FCSTD DOCUMENT  (FreeCAD 1.0RUnknown)
Label: wardrobe_corpus00_jan_assy4
License: All rights reserved
objects: App::Link×8, App::DocumentObjectGroup×3, Part::FeaturePython×3, PartDesign::CoordinateSystem×2, App::FeaturePython×1, App::Part×1
note: 5 computed .brp shape members not serialized (recipe doc carries the construction recipe); baked Part::Feature solids carry a one-line shape summary decoded from their .brp
EXTERNAL_REF file=parts/wardrobe_base_jan.FCStd obj=LCS_center
EXTERNAL_REF file=parts/wardrobe_base_jan.FCStd obj=Body
EXTERNAL_REF file=parts/wardrobe_base_jan.FCStd obj=LCS_1
EXTERNAL_REF file=parts/wardrobe_left_corpus00_jan.FCStd obj=LCS_bottom
EXTERNAL_REF file=parts/wardrobe_left_corpus00_jan.FCStd obj=Body001
EXTERNAL_REF file=parts/wardrobe_base_jan.FCStd obj=LCS_right
EXTERNAL_REF file=parts/wardrobe_right_corpus00_jan.FCStd obj=LCS_bottom
EXTERNAL_REF file=parts/wardrobe_right_corpus00_jan.FCStd obj=Body002
EXTERNAL_REF file=parts/wardrobe_left_corpus00_jan.FCStd obj=LCS_top
EXTERNAL_REF file=parts/wardrobe_top_jan.FCStd obj=LCS_left
EXTERNAL_REF file=parts/wardrobe_top_jan.FCStd obj=Body003
EXTERNAL_REF file=parts/wardrobe_backplate_corpus00_jan.FCStd obj=LCS_bottom
EXTERNAL_REF file=parts/wardrobe_base_jan.FCStd obj=LCS_back
EXTERNAL_REF file=parts/wardrobe_backplate_corpus00_jan.FCStd obj=Body004
EXTERNAL_REF file=parts/wardrobe_base_jan.FCStd obj=LCS_door
EXTERNAL_REF file=parts/wardrobe_door_corpus00_jan.FCStd obj=Body
EXTERNAL_REF file=wardrobe_drawer_jan_assy4.FCStd obj=LCS_Origin
EXTERNAL_REF file=parts/wardrobe_left_corpus00_jan.FCStd obj=LCS_inner_bottom
EXTERNAL_REF file=wardrobe_drawer_jan_assy4.FCStd obj=Assembly
EXTERNAL_REF file=../purchased parts/hettich-level-adjustment.FCStd obj=LCS_Origin
EXTERNAL_REF file=parts/wardrobe_base_jan.FCStd obj=LCS_2
EXTERNAL_REF file=../purchased parts/hettich-level-adjustment.FCStd obj=hettich_level_adjustment

FEATURE [App::DocumentObjectGroup] Parts
FEATURE [PartDesign::CoordinateSystem] LCS_Origin
  AttacherType = Attacher::AttachEngine3D
  AttachmentSupport = -> [X_Axis]
  MapMode = 2
FEATURE [App::DocumentObjectGroup] Constraints
FEATURE [App::FeaturePython] Variables  # WARN: FeaturePython — macro-defined, semantics opaque (R4)
  Type = App::PropertyContainer
FEATURE [App::DocumentObjectGroup] Configurations
FEATURE [App::Link] wardrobe_base_jan
  AttachedBy = #LCS_center
  AttachedTo = Parent Assembly#LCS_Origin
  LinkedObject = -> <external parts/wardrobe_base_jan.FCStd>#Body
  SolverId = Asm4EE
  expr: Placement = LCS_Origin.Placement * AttachmentOffset * wardrobe_base_jan#LCS_center.Placement ^ -1
FEATURE [App::Link] wardrobe_left_corpus00_jan
  AttachedBy = #LCS_bottom
  AttachedTo = wardrobe_base_jan#LCS_1
  LinkPlacement = pos=(-270,2.37e-13,1022.5) rot=(0,0,1;0rad)
  LinkedObject = -> <external parts/wardrobe_left_corpus00_jan.FCStd>#Body001
  Placement = pos=(-270,2.37e-13,1022.5) rot=(0,0,1;0rad)
  SolverId = Asm4EE
  expr: Placement = wardrobe_base_jan.Placement * wardrobe_base_jan#LCS_1.Placement * AttachmentOffset * wardrobe_left_corpus00_jan#LCS_bottom.Placement ^ -1
FEATURE [App::Link] wardrobe_right_corpus00_jan
  AttachedBy = #LCS_bottom
  AttachedTo = wardrobe_base_jan#LCS_right
  LinkPlacement = pos=(251,2.086e-13,1022.5) rot=(0,0,1;0rad)
  LinkedObject = -> <external parts/wardrobe_right_corpus00_jan.FCStd>#Body002
  Placement = pos=(251,2.086e-13,1022.5) rot=(0,0,1;0rad)
  SolverId = Asm4EE
  expr: Placement = wardrobe_base_jan.Placement * wardrobe_base_jan#LCS_right.Placement * AttachmentOffset * wardrobe_right_corpus00_jan#LCS_bottom.Placement ^ -1
FEATURE [App::Link] wardrobe_top_jan
  AttachedBy = #LCS_left
  AttachedTo = wardrobe_left_corpus00_jan#LCS_top
  LinkPlacement = pos=(-5.116e-13,3.858e-13,2026) rot=(0,0,1;0rad)
  LinkedObject = -> <external parts/wardrobe_top_jan.FCStd>#Body003
  Placement = pos=(-5.116e-13,3.858e-13,2026) rot=(0,0,1;0rad)
  SolverId = Asm4EE
  expr: Placement = wardrobe_left_corpus00_jan.Placement * wardrobe_left_corpus00_jan#LCS_top.Placement * AttachmentOffset * wardrobe_top_jan#LCS_left.Placement ^ -1
FEATURE [App::Link] wardrobe_backplate_corpus00_jan
  AttachedBy = #LCS_bottom
  AttachedTo = wardrobe_base_jan#LCS_back
  LinkPlacement = pos=(5.68e-14,319,1022.5) rot=(0,0,1;0rad)
  LinkedObject = -> <external parts/wardrobe_backplate_corpus00_jan.FCStd>#Body004
  Placement = pos=(5.68e-14,319,1022.5) rot=(0,0,1;0rad)
  SolverId = Asm4EE
  expr: Placement = wardrobe_base_jan.Placement * wardrobe_base_jan#LCS_back.Placement * AttachmentOffset * wardrobe_backplate_corpus00_jan#LCS_bottom.Placement ^ -1
FEATURE [App::Link] wardrobe_door_corpus00_jan
  AttachedBy = #LCS_right
  AttachedTo = wardrobe_base_jan#LCS_door
  AttachmentOffset = pos=(2.5,0,0) rot=(0,0,1;1.5708rad)
  LinkPlacement = pos=(267.5,-300,0) rot=(0.57735,0.57735,0.57735;2.0944rad)
  LinkedObject = -> <external parts/wardrobe_door_corpus00_jan.FCStd>#Body
  Placement = pos=(267.5,-300,0) rot=(0.57735,0.57735,0.57735;2.0944rad)
  SolverId = Asm4EE
  expr: Placement = wardrobe_base_jan.Placement * wardrobe_base_jan#LCS_door.Placement * AttachmentOffset * wardrobe_door_corpus00_jan#LCS_right.Placement ^ -1
FEATURE [App::Link] wardrobe_drawer_jan_assy4
  AttachedBy = #LCS_Origin
  AttachedTo = wardrobe_left_corpus00_jan#LCS_inner_bottom
  AttachmentOffset = pos=(0,20,0) rot=(0,0,1;1.5708rad)
  LinkPlacement = pos=(-251,2.232e-13,39) rot=(0.57735,0.57735,0.57735;4.18879rad)
  LinkedObject = -> <external wardrobe_drawer_jan_assy4.FCStd>#Assembly
  Placement = pos=(-251,2.232e-13,39) rot=(0.57735,0.57735,0.57735;4.18879rad)
  SolverId = Asm4EE
  expr: Placement = wardrobe_left_corpus00_jan.Placement * wardrobe_left_corpus00_jan#LCS_inner_bottom.Placement * AttachmentOffset * wardrobe_drawer_jan_assy4#LCS_Origin.Placement ^ -1
FEATURE [Part::FeaturePython] Linear_wardrobe_drawer_jan_assy4  # Draft array (typed FeaturePython)
  ArrayType = Linear Array
  Axis = -> Z_Axis
  AxisPlacement = pos=(0,0,0) rot=(0,0,1.73205;3.14159rad)
  Count = 6
  Index = 1
  LinearStep = 200
  PlacementList = 6 placements: arithmetic series from (-251,2.2323e-13,39) step (5.68434e-14,0,200) to (-251,2.2323e-13,1039)
  Placer = pos=(0,0,1000) rot=(0,0,1;0rad)
  ScaleList = (6) [(1,1,1),(1,1,1),(1,1,1),(1,1,1),(1,1,1),(1,1,1)]
  Scaler = 1
  ShowElement = false
  SourceObject = -> wardrobe_drawer_jan_assy4
  expr: .Placer.Base.z = LinearStep * Index
FEATURE [PartDesign::CoordinateSystem] LCS_003  label="LCS_1"
  AttacherType = Attacher::AttachEngine3D
FEATURE [App::Link] hettich_level_adjustment
  AttachedBy = #LCS_Origin
  AttachedTo = wardrobe_base_jan#LCS_2
  AttachmentOffset = pos=(0,0,0) rot=(0.707107,-0.707107,0;3.14159rad)
  LinkPlacement = pos=(-220,-230,0) rot=(0.707107,-0.707107,0;3.14159rad)
  LinkedObject = -> <external ../purchased parts/hettich-level-adjustment.FCStd>#hettich_level_adjustment
  Placement = pos=(-220,-230,0) rot=(0.707107,-0.707107,0;3.14159rad)
  SolverId = Asm4EE
  expr: Placement = wardrobe_base_jan.Placement * wardrobe_base_jan#LCS_2.Placement * AttachmentOffset * hettich_level_adjustment#LCS_Origin.Placement ^ -1
FEATURE [Part::FeaturePython] Linear_hettich_level_adjustment  # Draft array (typed FeaturePython)
  ArrayType = Linear Array
  Axis = -> X_Axis
  AxisPlacement = pos=(0,0,0) rot=(0.57735,0.57735,0.57735;2.0944rad)
  Count = 2
  Index = 1
  LinearStep = 440
  PlacementList = 2 placements: [(-220,-230,6.31089e-30),(220,-230,4.88498e-14)]
  Placer = pos=(0,0,440) rot=(0,0,1;0rad)
  ScaleList = (2) [(1,1,1),(1,1,1)]
  Scaler = 1
  ShowElement = false
  SourceObject = -> hettich_level_adjustment
  expr: .Placer.Base.z = LinearStep * Index
FEATURE [Part::FeaturePython] Linear_Linear_hettich_level_adjustment  # Draft array (typed FeaturePython)
  ArrayType = Linear Array
  Axis = -> Y_Axis
  AxisPlacement = pos=(0,0,0) rot=(1,1,1;4.18879rad)
  Count = 2
  Index = 1
  LinearStep = 460
  PlacementList = 2 placements: [(0,0,0),(5.10703e-14,460,-1.53211e-13)]
  Placer = pos=(0,0,460) rot=(0,0,1;0rad)
  ScaleList = (2) [(1,1,1),(1,1,1)]
  Scaler = 1
  ShowElement = false
  SourceObject = -> Linear_hettich_level_adjustment
  expr: .Placer.Base.z = LinearStep * Index
FEATURE [App::Part] Assembly  label="wardrobe_corpus00_jan"
  AssemblyType = Part::Link
  Group = -> [LCS_Origin,Constraints,Variables,Configurations,wardrobe_base_jan,wardrobe_left_corpus00_jan,wardrobe_right_corpus00_jan,wardrobe_top_jan,wardrobe_backplate_corpus00_jan,wardrobe_door_corpus00_jan,wardrobe_drawer_jan_assy4,Linear_wardrobe_drawer_jan_assy4,LCS_003,hettich_level_adjustment,Linear_hettich_level_adjustment,Linear_Linear_hettich_level_adjustment]
  Origin = -> Origin
  Type = Assembly

RESOLVED EXTERNAL PARTS (link-assembly join: the EXTERNAL_REF files above that resolve inside this repo's crawl, each included once):
---- part parts/wardrobe_backplate_corpus00_jan.FCStd = doc fcstd_ef48b797989f ----
FCSTD DOCUMENT  (FreeCAD 1.0RUnknown)
Label: wardrobe_backplate_corpus00_jan
License: All rights reserved
LicenseURL: https://en.wikipedia.org/wiki/All_rights_reserved
objects: PartDesign::CoordinateSystem×2, Sketcher::SketchObject×1, PartDesign::Pad×1, PartDesign::Body×1
note: 8 computed .brp shape members not serialized (recipe doc carries the construction recipe); baked Part::Feature solids carry a one-line shape summary decoded from their .brp
EXTERNAL_REF file=../../mastersketch.FCStd obj=Spreadsheet

FEATURE [Sketcher::SketchObject] Sketch004
  ArcFitTolerance = 1e-06
  AttachmentSupport = -> [XZ_Plane006]
  FullyConstrained = true
  MakeInternals = false
  MapMode = 5
  Placement = pos=(0,0,0) rot=(1,0,0;1.5708rad)
  expr: Constraints[10] = mastersketch#Spreadsheet.corpus_width
  expr: Constraints[11] = mastersketch#Spreadsheet.corpus_height
  sketch-geometry (5):
    g0: LineSegment StartX=-270 StartY=-1022.5 StartZ=0 EndX=270 EndY=-1022.5 EndZ=0
    g1: LineSegment StartX=270 StartY=-1022.5 StartZ=0 EndX=270 EndY=1022.5 EndZ=0
    g2: LineSegment StartX=270 StartY=1022.5 StartZ=0 EndX=-270 EndY=1022.5 EndZ=0
    g3: LineSegment StartX=-270 StartY=1022.5 StartZ=0 EndX=-270 EndY=-1022.5 EndZ=0
    g4: GeomPoint [constr] X=0 Y=0 Z=0
  constraints (12):
    c: Coincident(g0,g1)
    c: Coincident(g1,g2)
    c: Coincident(g2,g3)
    c: Coincident(g3,g0)
    c: Horizontal(g0)
    c: Horizontal(g2)
    c: Vertical(g1)
    c: Vertical(g3)
    c: Symmetric(g2,g0,g4)
    c: Coincident(g4,g-1)
    c: DistanceX(g0,g0) = 540
    c: DistanceY(g3,g3) = 2045
FEATURE [PartDesign::Pad] Pad004
  Direction = (0,-1,2e-16)
  Length = 19
  Length2 = 10
  Placement = pos=(0,0,0) rot=(1,0,0;1.5708rad)
  Profile = -> Sketch004
  ReferenceAxis = -> Sketch004 [N_Axis]
  Refine = true
  Suppressed = false
  Type = 0
  expr: Length = mastersketch#Spreadsheet.corpus_backplate_thickness
FEATURE [PartDesign::CoordinateSystem] LCS_bottom
  AttacherType = Attacher::AttachEngine3D
  AttachmentSupport = -> [Pad004]
  MapMode = 45
  Placement = pos=(0,-19,-1022.5) rot=(0.57735,0.57735,0.57735;2.0944rad)
FEATURE [PartDesign::CoordinateSystem] LCS_back_right
  AttacherType = Attacher::AttachEngine3D
FEATURE [PartDesign::Body] Body004  label="wardrobe_backplate_corpus00_jan"
  AllowCompound = false
  Group = -> [Sketch004,Pad004,LCS_bottom,LCS_back_right]
  Origin = -> Origin006
  Tip = -> Pad004
---- part parts/wardrobe_base_jan.FCStd = doc fcstd_ceb563eaf676 ----
FCSTD DOCUMENT  (FreeCAD 1.0RUnknown)
Label: wardrobe_base_jan
License: All rights reserved
LicenseURL: https://en.wikipedia.org/wiki/All_rights_reserved
objects: PartDesign::CoordinateSystem×9, Sketcher::SketchObject×2, PartDesign::Pad×1, PartDesign::Body×1
note: 17 computed .brp shape members not serialized (recipe doc carries the construction recipe); baked Part::Feature solids carry a one-line shape summary decoded from their .brp
EXTERNAL_REF file=../../mastersketch.FCStd obj=Spreadsheet

FEATURE [Sketcher::SketchObject] Sketch
  ArcFitTolerance = 1e-06
  AttachmentSupport = -> [XY_Plane]
  FullyConstrained = true
  MakeInternals = false
  MapMode = 5
  expr: Constraints[10] = mastersketch#Spreadsheet.corpus_width
  expr: Constraints[11] = mastersketch#Spreadsheet.corpus_depth
  sketch-geometry (5):
    g0: LineSegment StartX=-270 StartY=-300 StartZ=0 EndX=270 EndY=-300 EndZ=0
    g1: LineSegment StartX=270 StartY=-300 StartZ=0 EndX=270 EndY=300 EndZ=0
    g2: LineSegment StartX=270 StartY=300 StartZ=0 EndX=-270 EndY=300 EndZ=0
    g3: LineSegment StartX=-270 StartY=300 StartZ=0 EndX=-270 EndY=-300 EndZ=0
    g4: GeomPoint [constr] X=0 Y=0 Z=0
  constraints (12):
    c: Coincident(g0,g1)
    c: Coincident(g1,g2)
    c: Coincident(g2,g3)
    c: Coincident(g3,g0)
    c: Horizontal(g0)
    c: Horizontal(g2)
    c: Vertical(g1)
    c: Vertical(g3)
    c: Symmetric(g2,g0,g4)
    c: Coincident(g4,g-1)
    c: DistanceX(g0,g0) = 540
    c: DistanceY(g3,g3) = 600
FEATURE [PartDesign::Pad] Pad
  Direction = (0,0,1)
  Length = 19
  Length2 = 10
  Profile = -> Sketch
  ReferenceAxis = -> Sketch [N_Axis]
  Refine = true
  Suppressed = false
  Type = 0
  expr: Length = mastersketch#Spreadsheet.corpus_outer_thickness
FEATURE [PartDesign::CoordinateSystem] LCS_1  label="LCS_left"
  AttacherType = Attacher::AttachEngine3D
  AttachmentSupport = -> [Pad]
  MapMode = 45
  Placement = pos=(-270,1.42e-14,19) rot=(0,0.707107,0.707107;3.14159rad)
FEATURE [PartDesign::CoordinateSystem] LCS_right  label="LCS-right"
  AttacherType = Attacher::AttachEngine3D
  AttachmentSupport = -> [Pad]
  MapMode = 45
  Placement = pos=(270,-1.42e-14,19) rot=(0,0.707107,0.707107;3.14159rad)
FEATURE [PartDesign::CoordinateSystem] LCS_center
  AttacherType = Attacher::AttachEngine3D
FEATURE [Sketcher::SketchObject] Sketch_1  label="feet_placement"
  ArcFitTolerance = 1e-06
  AttachmentSupport = -> [Pad]
  FullyConstrained = true
  MakeInternals = false
  MapMode = 5
  Placement = pos=(0,0,0) rot=(1,0,0;3.14159rad)
  expr: Constraints[10] = mastersketch#Spreadsheet.corpus_width - 100
  expr: Constraints[11] = mastersketch#Spreadsheet.corpus_depth - 140
  sketch-geometry (5):
    g0: LineSegment StartX=-220 StartY=-230 StartZ=0 EndX=220 EndY=-230 EndZ=0
    g1: LineSegment StartX=220 StartY=-230 StartZ=0 EndX=220 EndY=230 EndZ=0
    g2: LineSegment StartX=220 StartY=230 StartZ=0 EndX=-220 EndY=230 EndZ=0
    g3: LineSegment StartX=-220 StartY=230 StartZ=0 EndX=-220 EndY=-230 EndZ=0
    g4: GeomPoint [constr] X=0 Y=0 Z=0
  constraints (12):
    c: Coincident(g0,g1)
    c: Coincident(g1,g2)
    c: Coincident(g2,g3)
    c: Coincident(g3,g0)
    c: Horizontal(g0)
    c: Horizontal(g2)
    c: Vertical(g1)
    c: Vertical(g3)
    c: Symmetric(g2,g0,g4)
    c: Coincident(g4,g-1)
    c: DistanceX(g0,g0) = 440
    c: DistanceY(g3,g3) = 460
FEATURE [PartDesign::CoordinateSystem] LCS_2  label="LCS_feet0"
  AttacherType = Attacher::AttachEngine3D
  AttachmentSupport = -> [Sketch_1]
  MapMode = 1
  Placement = pos=(-220,-230,0) rot=(0,0,1;0rad)
FEATURE [PartDesign::CoordinateSystem] LCS_feet1
  AttacherType = Attacher::AttachEngine3D
  AttachmentSupport = -> [Sketch_1]
  MapMode = 1
  Placement = pos=(220,-230,0) rot=(0,0,1;0rad)
FEATURE [PartDesign::CoordinateSystem] LCS_feet2
  AttacherType = Attacher::AttachEngine3D
  AttachmentSupport = -> [Sketch_1]
  MapMode = 1
  Placement = pos=(220,230,0) rot=(0,0,1;0rad)
FEATURE [PartDesign::CoordinateSystem] LCS_feet3
  AttacherType = Attacher::AttachEngine3D
  AttachmentSupport = -> [Sketch_1]
  MapMode = 1
  Placement = pos=(-220,230,0) rot=(0,0,1;0rad)
FEATURE [PartDesign::CoordinateSystem] LCS_back
  AttacherType = Attacher::AttachEngine3D
  AttachmentSupport = -> [Pad]
  MapMode = 45
  Placement = pos=(0,300,0) rot=(0.57735,0.57735,0.57735;2.0944rad)
FEATURE [PartDesign::CoordinateSystem] LCS_door
  AttacherType = Attacher::AttachEngine3D
  AttachmentSupport = -> [Pad]
  MapMode = 7
  Placement = pos=(270,-300,0) rot=(0,1,0;3.14159rad)
FEATURE [PartDesign::Body] Body  label="wardrobe_base_jan"
  AllowCompound = false
  Group = -> [Sketch,Pad,LCS_1,LCS_right,LCS_center,Sketch_1,LCS_2,LCS_feet1,LCS_feet2,LCS_feet3,LCS_back,LCS_door]
  Origin = -> Origin
  Tip = -> Pad
---- part parts/wardrobe_door_corpus00_jan.FCStd = doc fcstd_de45f609bab9 ----
FCSTD DOCUMENT  (FreeCAD 1.0R39285 (Git))
Label: wardrobe_door_corpus00_jan
License: All rights reserved
LicenseURL: https://en.wikipedia.org/wiki/All_rights_reserved
objects: TechDraw::DrawViewDimension×7, PartDesign::CoordinateSystem×2, TechDraw::DrawProjGroupItem×2, Sketcher::SketchObject×1, PartDesign::Pad×1, PartDesign::Body×1, TechDraw::DrawSVGTemplate×1, TechDraw::DrawViewAnnotation×1, App::Part×1, TechDraw::DrawPage×1
note: 17 computed .brp shape members not serialized (recipe doc carries the construction recipe); baked Part::Feature solids carry a one-line shape summary decoded from their .brp
EXTERNAL_REF file=../../mastersheet.FCStd obj=Spreadsheet
EXTERNAL_REF file=../../mastersketch.FCStd obj=Sketch

FEATURE [Sketcher::SketchObject] Sketch
  ArcFitTolerance = 1e-06
  AttachmentSupport = -> [XY_Plane]
  FullyConstrained = true
  MakeInternals = false
  MapMode = 5
  expr: Constraints[0] = mastersketch#Sketch.Constraints.corpus00_door_height
  expr: Constraints[12] = mastersketch#Sketch.Constraints.alpha
  expr: Constraints[13] = mastersketch#Sketch.Constraints.corpus00_door_top
  expr: Constraints[5] = mastersheet#Spreadsheet.corpus_width - 5
  sketch-geometry (5):
    g0: LineSegment StartX=0 StartY=0 StartZ=0 EndX=0 EndY=2440 EndZ=0
    g1: LineSegment StartX=0 StartY=2440 StartZ=0 EndX=-202.892 EndY=2440 EndZ=0
    g2: LineSegment StartX=0 StartY=0 StartZ=0 EndX=-535 EndY=0 EndZ=0
    g3: LineSegment StartX=-535 StartY=0 StartZ=0 EndX=-535 EndY=2051.4 EndZ=0
    g4: LineSegment StartX=-535 StartY=2051.4 StartZ=0 EndX=-202.892 EndY=2440 EndZ=0
  constraints (14):
    c: Distance(g0) = 2440
    c: Coincident(g0,g-1)
    c: Vertical(g0)
    c: Coincident(g1,g0)
    c: Horizontal(g1)
    c: Distance(g2) = 535
    c: Coincident(g2,g0)
    c: PointOnObject(g2,g-1)
    c: Vertical(g3)
    c: Coincident(g4,g1)
    c: Coincident(g4,g3)
    c: Coincident(g3,g2)
    c: Angle(g3,g4) = 2.43442
    c: DistanceX(g1,g1) = 202.892
FEATURE [PartDesign::Pad] Pad
  Direction = (0,0,1)
  Length = 19
  Length2 = 10
  Profile = -> Sketch
  ReferenceAxis = -> Sketch [N_Axis]
  Refine = true
  Suppressed = false
  Type = 0
FEATURE [PartDesign::Body] Body  label="wardrobe_door_corpus00_jan"
  AllowCompound = false
  Group = -> [Sketch,Pad]
  Origin = -> Origin
  Tip = -> Pad
FEATURE [PartDesign::CoordinateSystem] LCS_right
  AttacherType = Attacher::AttachEngine3D
  AttachmentSupport = -> [Pad]
  MapMode = 7
  Placement = pos=(0,0,0) rot=(1,0,0;1.5708rad)
FEATURE [TechDraw::DrawSVGTemplate] Template  label="Vorlage"
  Height = 210
  Orientation = 1
  Template = <userpath>/scoop/apps/freecad/current/data/Mod/TechDraw/Templates/A4_Landscape_TD.svg
  Width = 297
FEATURE [TechDraw::DrawProjGroupItem] View  label="Oben"
  CoarseView = false
  Direction = (0,0,-1)
  Focus = 100
  HardHidden = false
  IsoCount = 0
  IsoHidden = false
  IsoVisible = false
  LockPosition = false
  Perspective = false
  Rotation = 0
  RotationVector = (1,0,0)
  Scale = 0.1
  ScaleType = 2
  ScrubCount = 1
  SeamHidden = false
  SeamVisible = false
  SmoothHidden = false
  SmoothVisible = true
  Source = -> [Body]
  Type = 0
  X = 142.185
  XDirection = (1e-16,-1,0)
  Y = 151.82
FEATURE [TechDraw::DrawProjGroupItem] View001  label="Seite"
  CoarseView = false
  Direction = (-1,-1e-16,0)
  Focus = 100
  HardHidden = false
  IsoCount = 0
  IsoHidden = false
  IsoVisible = false
  LockPosition = false
  Perspective = false
  Rotation = 0
  RotationVector = (1,0,0)
  Scale = 0.1
  ScaleType = 2
  ScrubCount = 1
  SeamHidden = false
  SeamVisible = false
  SmoothHidden = false
  SmoothVisible = true
  Source = -> [Body]
  Type = 0
  X = 143.628
  XDirection = (1e-16,-1,0)
  Y = 90.5756
FEATURE [TechDraw::DrawViewDimension] Dimension  label="Maß"
  AngleOverride = false
  Arbitrary = false
  ArbitraryTolerances = false
  BoxCorners = (2) [(-122,-26.75,0),(122,26.75,0)]
  EqualTolerance = true
  ExtensionAngle = 0
  FormatSpec = %.2w
  FormatSpecOverTolerance = %+.2w
  FormatSpecUnderTolerance = %+.2w
  Inverted = false
  LineAngle = 0
  LockPosition = false
  MeasureType = 1
  OverTolerance = 0
  References2D = -> [View]
  Rotation = 0
  ScaleType = 0
  TheoreticalExact = false
  Type = 0
  UnderTolerance = 0
  X = 129.212
  Y = 0
FEATURE [TechDraw::DrawViewDimension] Dimension001  label="Maß001"
  AngleOverride = false
  Arbitrary = false
  ArbitraryTolerances = false
  BoxCorners = (2) [(-122,-26.75,0),(122,26.75,0)]
  EqualTolerance = true
  ExtensionAngle = 0
  FormatSpec = %.2w
  FormatSpecOverTolerance = %+.2w
  FormatSpecUnderTolerance = %+.2w
  Inverted = false
  LineAngle = 0
  LockPosition = false
  MeasureType = 1
  OverTolerance = 0
  References2D = -> [View]
  Rotation = 0
  ScaleType = 0
  TheoreticalExact = false
  Type = 1
  UnderTolerance = 0
  X = 0
  Y = -32.8109
FEATURE [TechDraw::DrawViewDimension] Dimension002  label="Maß002"
  AngleOverride = false
  Arbitrary = false
  ArbitraryTolerances = false
  BoxCorners = (2) [(-122,-26.75,0),(122,26.75,0)]
  EqualTolerance = true
  ExtensionAngle = 0
  FormatSpec = %.2w
  FormatSpecOverTolerance = %+.2w
  FormatSpecUnderTolerance = %+.2w
  Inverted = false
  LineAngle = 0
  LockPosition = false
  MeasureType = 1
  OverTolerance = 0
  References2D = -> [View]
  Rotation = 0
  ScaleType = 0
  TheoreticalExact = false
  Type = 1
  UnderTolerance = 0
  X = 19.43
  Y = 40.4934
FEATURE [TechDraw::DrawViewDimension] Dimension003  label="Maß003"
  AngleOverride = false
  Arbitrary = false
  ArbitraryTolerances = false
  BoxCorners = (2) [(-122,-26.75,0),(122,26.75,0)]
  EqualTolerance = true
  ExtensionAngle = 0
  FormatSpec = %.1w
  FormatSpecOverTolerance = %+.2w
  FormatSpecUnderTolerance = %+.2w
  Inverted = false
  LineAngle = 0
  LockPosition = false
  MeasureType = 1
  OverTolerance = 0
  References2D = -> [View]
  Rotation = 0
  ScaleType = 0
  TheoreticalExact = false
  Type = 2
  UnderTolerance = 0
  X = -102.279
  Y = -16.6054
FEATURE [TechDraw::DrawViewDimension] Dimension004  label="Maß004"
  AngleOverride = false
  Arbitrary = false
  ArbitraryTolerances = false
  BoxCorners = (2) [(-122,-0.9,0),(122,0.9,0)]
  EqualTolerance = true
  ExtensionAngle = 0
  FormatSpec = %.2w
  FormatSpecOverTolerance = %+.2w
  FormatSpecUnderTolerance = %+.2w
  Inverted = false
  LineAngle = 0
  LockPosition = false
  MeasureType = 1
  OverTolerance = 0
  References2D = -> [View001]
  Rotation = 0
  ScaleType = 0
  TheoreticalExact = false
  Type = 0
  UnderTolerance = 0
  X = 124.097
  Y = -13.7815
FEATURE [TechDraw::DrawViewDimension] Dimension005  label="Maß005"
  AngleOverride = false
  Arbitrary = false
  ArbitraryTolerances = false
  BoxCorners = (2) [(-122,-26.75,0),(122,26.75,0)]
  EqualTolerance = true
  ExtensionAngle = 0
  FormatSpec = (%.1w)
  FormatSpecOverTolerance = %+.1w
  FormatSpecUnderTolerance = %+.1w
  Inverted = false
  LineAngle = 0
  LockPosition = false
  MeasureType = 1
  OverTolerance = 0
  References2D = -> [View]
  Rotation = 0
  ScaleType = 0
  TheoreticalExact = false
  Type = 6
  UnderTolerance = 0
  X = -75.6861
  Y = 12.9628
FEATURE [TechDraw::DrawViewAnnotation] Annotation  label="Beschriftung"
  Font = MS Shell Dlg 2
  LineSpace = 100
  LockPosition = false
  MaxWidth = -1
  Rotation = 0
  ScaleType = 0
  Text = Rev 01
  TextSize = 5
  TextStyle = 0
  X = 271.909
  Y = 62.045
FEATURE [PartDesign::CoordinateSystem] LCS_Origin
  AttacherType = Attacher::AttachEngine3D
  AttachmentSupport = -> [X_Axis001]
  MapMode = 2
FEATURE [App::Part] wardrobe_door_corpus00_jan  label="wardrobe_door_corpus00_jan001"
  DrawingName = wardrobe_door_corpus00_jan.FCStd
  Group = -> [LCS_Origin,LCS_right,Body]
  Origin = -> Origin001
  PartDescription = wardrobe_door_corpus00_jan
  PartID = wardrobe_door_corpus00_jan
FEATURE [TechDraw::DrawViewDimension] Dimension006  label="Maß006"
  AngleOverride = false
  Arbitrary = false
  ArbitraryTolerances = false
  BoxCorners = (2) [(-122,-26.75,0),(122,26.75,0)]
  EqualTolerance = true
  ExtensionAngle = 0
  FormatSpec = (%.1w)
  FormatSpecOverTolerance = %+.1w
  FormatSpecUnderTolerance = %+.1w
  Inverted = false
  LineAngle = 0
  LockPosition = false
  MeasureType = 1
  OverTolerance = 0
  References2D = -> [View]
  Rotation = 0
  ScaleType = 0
  TheoreticalExact = false
  Type = 0
  UnderTolerance = 0
  X = -112.05
  Y = 21.2372
FEATURE [TechDraw::DrawPage] Page  label="Drawing"
  KeepUpdated = true
  NextBalloonIndex = 1
  ProjectionType = 0
  Template = -> Template
  Views = -> [View,View001,Dimension,Dimension001,Dimension002,Dimension003,Dimension004,Dimension005,Annotation,Dimension006]
---- part parts/wardrobe_left_corpus00_jan.FCStd = doc fcstd_2dbd62044285 ----
FCSTD DOCUMENT  (FreeCAD 1.0RUnknown)
Label: wardrobe_left_corpus00_jan
License: All rights reserved
LicenseURL: https://en.wikipedia.org/wiki/All_rights_reserved
objects: PartDesign::CoordinateSystem×3, Sketcher::SketchObject×1, PartDesign::Pad×1, PartDesign::Body×1
note: 9 computed .brp shape members not serialized (recipe doc carries the construction recipe); baked Part::Feature solids carry a one-line shape summary decoded from their .brp
EXTERNAL_REF file=../../mastersketch.FCStd obj=Spreadsheet

FEATURE [Sketcher::SketchObject] Sketch001
  ArcFitTolerance = 1e-06
  AttachmentSupport = -> [YZ_Plane001]
  FullyConstrained = true
  MakeInternals = false
  MapMode = 5
  Placement = pos=(0,0,0) rot=(0.57735,0.57735,0.57735;2.0944rad)
  expr: Constraints[10] = mastersketch#Spreadsheet.corpus_depth
  expr: Constraints[11] = mastersketch#Spreadsheet.corpus_height - 2 * mastersketch#Spreadsheet.corpus_outer_thickness
  sketch-geometry (5):
    g0: LineSegment StartX=-300 StartY=-1003.5 StartZ=0 EndX=300 EndY=-1003.5 EndZ=0
    g1: LineSegment StartX=300 StartY=-1003.5 StartZ=0 EndX=300 EndY=1003.5 EndZ=0
    g2: LineSegment StartX=300 StartY=1003.5 StartZ=0 EndX=-300 EndY=1003.5 EndZ=0
    g3: LineSegment StartX=-300 StartY=1003.5 StartZ=0 EndX=-300 EndY=-1003.5 EndZ=0
    g4: GeomPoint [constr] X=0 Y=0 Z=0
  constraints (12):
    c: Coincident(g0,g1)
    c: Coincident(g1,g2)
    c: Coincident(g2,g3)
    c: Coincident(g3,g0)
    c: Horizontal(g0)
    c: Horizontal(g2)
    c: Vertical(g1)
    c: Vertical(g3)
    c: Symmetric(g2,g0,g4)
    c: Coincident(g4,g-1)
    c: DistanceX(g0,g0) = 600
    c: DistanceY(g3,g3) = 2007
FEATURE [PartDesign::Pad] Pad001
  Direction = (1,0,0)
  Length = 19
  Length2 = 10
  Placement = pos=(0,0,0) rot=(1,1,1;2.0944rad)
  Profile = -> Sketch001
  ReferenceAxis = -> Sketch001 [N_Axis]
  Refine = true
  Suppressed = false
  Type = 0
  expr: Length = mastersketch#Spreadsheet.corpus_outer_thickness
FEATURE [PartDesign::CoordinateSystem] LCS_bottom
  AttacherType = Attacher::AttachEngine3D
  AttachmentSupport = -> [Pad001]
  MapMode = 45
  Placement = pos=(0,-1.42e-14,-1003.5) rot=(0,0.707107,0.707107;3.14159rad)
FEATURE [PartDesign::CoordinateSystem] LCS_top
  AttacherType = Attacher::AttachEngine3D
  AttachmentSupport = -> [Pad001]
  MapMode = 45
  Placement = pos=(0,1.42e-14,1003.5) rot=(0,0.707107,0.707107;3.14159rad)
FEATURE [PartDesign::CoordinateSystem] LCS_inner_bottom
  AttacherType = Attacher::AttachEngine3D
  AttachmentSupport = -> [Pad001]
  MapMode = 45
  Placement = pos=(19,-1.82e-14,-1003.5) rot=(0,0.707107,0.707107;3.14159rad)
FEATURE [PartDesign::Body] Body001  label="wardrobe_left_corpus00_jan"
  AllowCompound = false
  Group = -> [Sketch001,Pad001,LCS_bottom,LCS_top,LCS_inner_bottom]
  Origin = -> Origin001
  Tip = -> Pad001
---- part parts/wardrobe_right_corpus00_jan.FCStd = doc fcstd_c843c1e678e7 ----
FCSTD DOCUMENT  (FreeCAD 1.0RUnknown)
Label: wardrobe_right_corpus00_jan
License: All rights reserved
LicenseURL: https://en.wikipedia.org/wiki/All_rights_reserved
objects: Sketcher::SketchObject×1, PartDesign::Pad×1, PartDesign::CoordinateSystem×1, PartDesign::Body×1
note: 7 computed .brp shape members not serialized (recipe doc carries the construction recipe); baked Part::Feature solids carry a one-line shape summary decoded from their .brp
EXTERNAL_REF file=../../mastersketch.FCStd obj=Spreadsheet

FEATURE [Sketcher::SketchObject] Sketch002
  ArcFitTolerance = 1e-06
  AttachmentSupport = -> [YZ_Plane004]
  FullyConstrained = true
  MakeInternals = true
  MapMode = 5
  Placement = pos=(0,0,0) rot=(0.57735,0.57735,0.57735;2.0944rad)
  expr: Constraints[10] = mastersketch#Spreadsheet.corpus_depth
  expr: Constraints[11] = mastersketch#Spreadsheet.corpus_height - 2 * mastersketch#Spreadsheet.corpus_outer_thickness
  sketch-geometry (5):
    g0: LineSegment StartX=-300 StartY=-1003.5 StartZ=0 EndX=300 EndY=-1003.5 EndZ=0
    g1: LineSegment StartX=300 StartY=-1003.5 StartZ=0 EndX=300 EndY=1003.5 EndZ=0
    g2: LineSegment StartX=300 StartY=1003.5 StartZ=0 EndX=-300 EndY=1003.5 EndZ=0
    g3: LineSegment StartX=-300 StartY=1003.5 StartZ=0 EndX=-300 EndY=-1003.5 EndZ=0
    g4: GeomPoint [constr] X=0 Y=0 Z=0
  constraints (12):
    c: Coincident(g0,g1)
    c: Coincident(g1,g2)
    c: Coincident(g2,g3)
    c: Coincident(g3,g0)
    c: Horizontal(g0)
    c: Horizontal(g2)
    c: Vertical(g1)
    c: Vertical(g3)
    c: Symmetric(g2,g0,g4)
    c: Coincident(g4,g-1)
    c: DistanceX(g0,g0) = 600
    c: DistanceY(g3,g3) = 2007
FEATURE [PartDesign::Pad] Pad002
  Direction = (1,0,0)
  Length = 19
  Length2 = 10
  Placement = pos=(0,0,0) rot=(1,1,1;2.0944rad)
  Profile = -> Sketch002
  ReferenceAxis = -> Sketch002 [N_Axis]
  Refine = true
  Suppressed = false
  Type = 0
  expr: Length = mastersketch#Spreadsheet.corpus_outer_thickness
FEATURE [PartDesign::CoordinateSystem] LCS_bottom
  AttacherType = Attacher::AttachEngine3D
  AttachmentSupport = -> [Pad002]
  MapMode = 45
  Placement = pos=(19,-1.82e-14,-1003.5) rot=(0,0.707107,0.707107;3.14159rad)
FEATURE [PartDesign::Body] Body002  label="wardrobe_right_corpus00_jan"
  AllowCompound = false
  Group = -> [Sketch002,Pad002,LCS_bottom]
  Origin = -> Origin004
  Tip = -> Pad002
---- part parts/wardrobe_top_jan.FCStd = doc fcstd_5a1df6a9867d ----
FCSTD DOCUMENT  (FreeCAD 1.0RUnknown)
Label: wardrobe_top_jan
License: All rights reserved
LicenseURL: https://en.wikipedia.org/wiki/All_rights_reserved
objects: Sketcher::SketchObject×1, PartDesign::Pad×1, PartDesign::CoordinateSystem×1, PartDesign::Body×1
note: 7 computed .brp shape members not serialized (recipe doc carries the construction recipe); baked Part::Feature solids carry a one-line shape summary decoded from their .brp
EXTERNAL_REF file=../../mastersketch.FCStd obj=Spreadsheet

FEATURE [Sketcher::SketchObject] Sketch003
  ArcFitTolerance = 1e-06
  AttachmentSupport = -> [XY_Plane005]
  FullyConstrained = true
  MakeInternals = false
  MapMode = 5
  expr: Constraints[10] = mastersketch#Spreadsheet.corpus_width
  expr: Constraints[11] = mastersketch#Spreadsheet.corpus_depth
  sketch-geometry (5):
    g0: LineSegment StartX=-270 StartY=-300 StartZ=0 EndX=270 EndY=-300 EndZ=0
    g1: LineSegment StartX=270 StartY=-300 StartZ=0 EndX=270 EndY=300 EndZ=0
    g2: LineSegment StartX=270 StartY=300 StartZ=0 EndX=-270 EndY=300 EndZ=0
    g3: LineSegment StartX=-270 StartY=300 StartZ=0 EndX=-270 EndY=-300 EndZ=0
    g4: GeomPoint [constr] X=0 Y=0 Z=0
  constraints (12):
    c: Coincident(g0,g1)
    c: Coincident(g1,g2)
    c: Coincident(g2,g3)
    c: Coincident(g3,g0)
    c: Horizontal(g0)
    c: Horizontal(g2)
    c: Vertical(g1)
    c: Vertical(g3)
    c: Symmetric(g2,g0,g4)
    c: Coincident(g4,g-1)
    c: DistanceX(g0,g0) = 540
    c: DistanceY(g3,g3) = 600
FEATURE [PartDesign::Pad] Pad003
  Direction = (0,0,1)
  Length = 19
  Length2 = 10
  Profile = -> Sketch003
  ReferenceAxis = -> Sketch003 [N_Axis]
  Refine = true
  Suppressed = false
  Type = 0
  expr: Length = mastersketch#Spreadsheet.corpus_outer_thickness
FEATURE [PartDesign::CoordinateSystem] LCS_left
  AttacherType = Attacher::AttachEngine3D
  AttachmentSupport = -> [Pad003]
  MapMode = 45
  Placement = pos=(-270,1.42e-14,0) rot=(0,0.707107,0.707107;3.14159rad)
FEATURE [PartDesign::Body] Body003  label="wardrobe_top_jan"
  AllowCompound = false
  Group = -> [Sketch003,Pad003,LCS_left]
  Origin = -> Origin005
  Tip = -> Pad003
---- part wardrobe_drawer_jan_assy4.FCStd = doc fcstd_a2e1da6712a3 ----
FCSTD DOCUMENT  (FreeCAD 1.0RUnknown)
Label: wardrobe_drawer_jan_assy4
License: All rights reserved
objects: App::Link×7, App::DocumentObjectGroup×4, PartDesign::CoordinateSystem×1, App::FeaturePython×1, App::Part×1
note: 1 computed .brp shape members not serialized (recipe doc carries the construction recipe); baked Part::Feature solids carry a one-line shape summary decoded from their .brp
EXTERNAL_REF file=../purchased parts/hettich_rail_550mm.FCStd obj=LCS_left_center
EXTERNAL_REF file=../purchased parts/hettich_rail_550mm.FCStd obj=Body
EXTERNAL_REF file=parts/drawer_sides.FCStd obj=LCS_bottom_center
EXTERNAL_REF file=../purchased parts/hettich_rail_550mm.FCStd obj=LCS_inner_center
EXTERNAL_REF file=parts/drawer_sides.FCStd obj=Body
EXTERNAL_REF file=parts/drawer_front.FCStd obj=LCS_left
EXTERNAL_REF file=parts/drawer_sides.FCStd obj=LCS_1
EXTERNAL_REF file=parts/drawer_front.FCStd obj=Body
EXTERNAL_REF file=parts/drawer_front.FCStd obj=LCS_right
EXTERNAL_REF file=parts/drawer_sides.FCStd obj=LCS_2
EXTERNAL_REF file=parts/drawer_bottom.FCStd obj=LCS_front
EXTERNAL_REF file=parts/drawer_front.FCStd obj=LCS_bottom_center
EXTERNAL_REF file=parts/drawer_bottom.FCStd obj=Body
EXTERNAL_REF file=parts/drawer_back.FCStd obj=LCS_left
EXTERNAL_REF file=parts/drawer_back.FCStd obj=Body

FEATURE [App::DocumentObjectGroup] Parts
FEATURE [PartDesign::CoordinateSystem] LCS_Origin
  AttacherType = Attacher::AttachEngine3D
  AttachmentSupport = -> [X_Axis]
  MapMode = 2
FEATURE [App::DocumentObjectGroup] Constraints
FEATURE [App::FeaturePython] Variables  # WARN: FeaturePython — macro-defined, semantics opaque (R4)
  Type = App::PropertyContainer
FEATURE [App::DocumentObjectGroup] Configurations
FEATURE [App::Link] hettich_rail_550
  AttachedBy = #LCS_left_center
  AttachedTo = Parent Assembly#LCS_Origin
  LinkPlacement = pos=(17.5,-9e-16,-1.6e-14) rot=(-0.57735,-0.57735,-0.57735;2.0944rad)
  LinkedObject = -> <external ../purchased parts/hettich_rail_550mm.FCStd>#Body
  Placement = pos=(17.5,-9e-16,-1.6e-14) rot=(-0.57735,-0.57735,-0.57735;2.0944rad)
  SolverId = Asm4EE
  expr: Placement = LCS_Origin.Placement * AttachmentOffset * hettich_rail_550mm#LCS_left_center.Placement ^ -1
FEATURE [App::Link] drawer_sides
  AttachedBy = #LCS_bottom_center
  AttachedTo = hettich_rail_550#LCS_inner_center
  AttachmentOffset = pos=(0,0,0) rot=(0,0,1;4.71239rad)
  LinkPlacement = pos=(90,22,256) rot=(0.57735,0.57735,0.57735;2.0944rad)
  LinkedObject = -> <external parts/drawer_sides.FCStd>#Body
  Placement = pos=(90,22,256) rot=(0.57735,0.57735,0.57735;2.0944rad)
  SolverId = Asm4EE
  expr: Placement = hettich_rail_550.Placement * hettich_rail_550mm#LCS_inner_center.Placement * AttachmentOffset * drawer_sides#LCS_bottom_center.Placement ^ -1
FEATURE [App::Link] drawer_front
  AttachedBy = #LCS_left
  AttachedTo = drawer_sides#LCS_1
  AttachmentOffset = pos=(0,0,0) rot=(0.707107,-0.707107,0;3.14159rad)
  LinkPlacement = pos=(90,12.5,-265.5) rot=(-0.707107,0,-0.707107;3.14159rad)
  LinkedObject = -> <external parts/drawer_front.FCStd>#Body
  Placement = pos=(90,12.5,-265.5) rot=(-0.707107,0,-0.707107;3.14159rad)
  SolverId = Asm4EE
  expr: Placement = drawer_sides.Placement * drawer_sides#LCS_1.Placement * AttachmentOffset * drawer_front#LCS_left.Placement ^ -1
FEATURE [App::Link] drawer_sides001
  AttachedBy = #LCS_2
  AttachedTo = drawer_front#LCS_right
  AttachmentOffset = pos=(0,0,0) rot=(0.707107,0.707107,0;3.14159rad)
  LinkPlacement = pos=(90,480,-256) rot=(0.57735,-0.57735,0.57735;4.18879rad)
  LinkedObject = -> <external parts/drawer_sides.FCStd>#Body
  Placement = pos=(90,480,-256) rot=(0.57735,-0.57735,0.57735;4.18879rad)
  SolverId = Asm4EE
  expr: Placement = drawer_front.Placement * drawer_front#LCS_right.Placement * AttachmentOffset * drawer_sides#LCS_2.Placement ^ -1
FEATURE [App::Link] drawer_bottom
  AttachedBy = #LCS_front
  AttachedTo = drawer_front#LCS_bottom_center
  AttachmentOffset = pos=(0,0,0) rot=(0,1,0;3.14159rad)
  LinkPlacement = pos=(15,251,5.75) rot=(0.57735,0.57735,0.57735;2.0944rad)
  LinkedObject = -> <external parts/drawer_bottom.FCStd>#Body
  Placement = pos=(15,251,5.75) rot=(0.57735,0.57735,0.57735;2.0944rad)
  SolverId = Asm4EE
  expr: Placement = drawer_front.Placement * drawer_front#LCS_bottom_center.Placement * AttachmentOffset * drawer_bottom#LCS_front.Placement ^ -1
FEATURE [App::Link] drawer_back
  AttachedBy = #LCS_left
  AttachedTo = drawer_sides#LCS_2
  AttachmentOffset = pos=(0,0,0) rot=(0.707107,0.707107,0;3.14159rad)
  LinkPlacement = pos=(98.25,489.5,265.5) rot=(0,1,0;1.5708rad)
  LinkedObject = -> <external parts/drawer_back.FCStd>#Body
  Placement = pos=(98.25,489.5,265.5) rot=(0,1,0;1.5708rad)
  SolverId = Asm4EE
  expr: Placement = drawer_sides.Placement * drawer_sides#LCS_2.Placement * AttachmentOffset * drawer_back#LCS_left.Placement ^ -1
FEATURE [App::Link] hettich_rail_551
  AttachedBy = #LCS_inner_center
  AttachedTo = drawer_sides001#LCS_bottom_center
  AttachmentOffset = pos=(0,0,0) rot=(0,0,1;1.5708rad)
  LinkPlacement = pos=(17.5,502,9.73e-14) rot=(-0.57735,-0.57735,0.57735;4.18879rad)
  LinkedObject = -> <external ../purchased parts/hettich_rail_550mm.FCStd>#Body
  Placement = pos=(17.5,502,9.73e-14) rot=(-0.57735,-0.57735,0.57735;4.18879rad)
  SolverId = Asm4EE
  expr: Placement = drawer_sides001.Placement * drawer_sides#LCS_bottom_center.Placement * AttachmentOffset * hettich_rail_550mm#LCS_inner_center.Placement ^ -1
FEATURE [App::Part] Assembly  label="wardrobe_drawer_jan_assy4"
  AssemblyType = Part::Link
  Group = -> [LCS_Origin,Constraints,Variables,Configurations,hettich_rail_550,drawer_sides,drawer_front,drawer_sides001,drawer_bottom,drawer_back,hettich_rail_551]
  Origin = -> Origin
  Type = Assembly
FEATURE [App::DocumentObjectGroup] Group  label="Gruppe"
